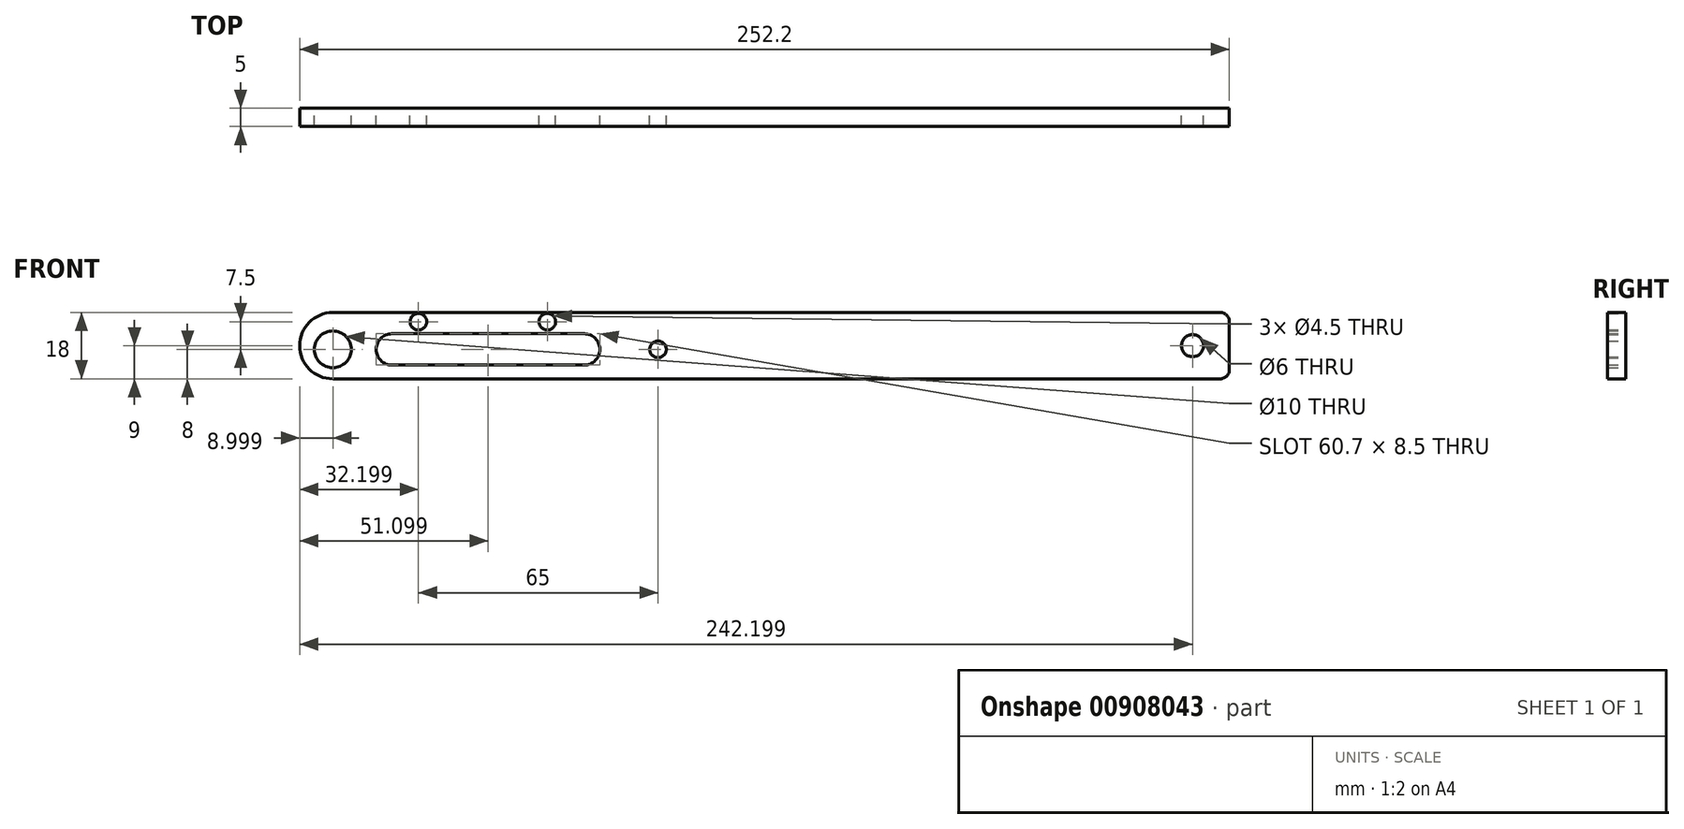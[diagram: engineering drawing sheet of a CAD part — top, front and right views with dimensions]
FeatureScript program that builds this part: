
annotation { "Feature Type Name" : "Feature", "Feature Type Description" : "" }
export const myFeature = defineFeature(function(context is Context, id is Id, definition is map)
    precondition{}
    {
        {
            var Q0;
            Q0=qCreatedBy(makeId("Front.planeOp"),FACE);
            var sketch = newSketch(context, id + "F0", { "sketchPlane" : qUnion([Q0])});
            skCircle(sketch, "E0", {"center": v(-38.63, 0) * mm, "radius": 5 * mm});
            skPoint(sketch, "E1", {"position": v(-22.63, 0) * mm});
            skPoint(sketch, "E2", {"position": v(29.57, 0) * mm});
            skPoint(sketch, "E3.middle", {"position": v(0, 0) * mm});
            skPoint(sketch, "E4", {"position": v(-38.63, 10) * mm});
            skPoint(sketch, "E5", {"position": v(-38.63, -8) * mm});
            skArc(sketch, "E6", {"start": v(-38.63, 10) * mm, "mid": v(-47.63, 1) * mm, "end": v(-38.63, -8) * mm});
            skCircle(sketch, "E7", {"center": v(49.57, 0) * mm, "radius": 2.25 * mm});
            skCircle(sketch, "E8", {"center": v(19.57, 7.5) * mm, "radius": 2.25 * mm});
            skCircle(sketch, "E9", {"center": v(-15.43, 7.5) * mm, "radius": 2.25 * mm});
            skArc(sketch, "E10", {"start": v(-22.63, 4.25) * mm, "mid": v(-26.88, 0) * mm, "end": v(-22.63, -4.25) * mm});
            skArc(sketch, "E11", {"start": v(29.57, -4.25) * mm, "mid": v(33.82, 0) * mm, "end": v(29.57, 4.25) * mm});
            skLineSegment(sketch, "E12.top", {"start": v(-22.63, 4.25) * mm, "end": v(29.57, 4.25) * mm});
            skLineSegment(sketch, "E13.top", {"start": v(-22.63, -4.25) * mm, "end": v(29.57, -4.25) * mm});
            skLineSegment(sketch, "E14.right", {"start": v(204.57, 7.5) * mm, "end": v(204.57, -5.5) * mm});
            skCircle(sketch, "E15", {"center": v(194.57, 1) * mm, "radius": 3 * mm});
            skPoint(sketch, "E15.centerSnap0", {"position": v(204.57, 1) * mm});
            skLineSegment(sketch, "E16", {"start": v(-38.63, -8) * mm, "end": v(202.07, -8) * mm});
            skLineSegment(sketch, "E17", {"start": v(-38.63, 10) * mm, "end": v(202.07, 10) * mm});
            skPoint(sketch, "E18", {"position": v(202.07, -5.5) * mm});
            skPoint(sketch, "E19", {"position": v(202.07, 7.5) * mm});
            skArc(sketch, "E20", {"start": v(204.57, 7.5) * mm, "mid": v(203.84, 9.27) * mm, "end": v(202.07, 10) * mm});
            skArc(sketch, "E21", {"start": v(202.07, -8) * mm, "mid": v(203.84, -7.27) * mm, "end": v(204.57, -5.5) * mm});
            skPoint(sketch, "E22.orphan", {"position": v(204.57, 10) * mm});
            skPoint(sketch, "E23.orphan", {"position": v(204.57, -8) * mm});
            skSolve(sketch);
        }
        {
            var Q0;
            Q0=qSketchRegion(id+"F0",true);
            extrude(context, id + "F1", {"entities" : qUnion([Q0]), "depth" : 5 * mm, "offsetDistance" : 25 * mm});
        }
    });
